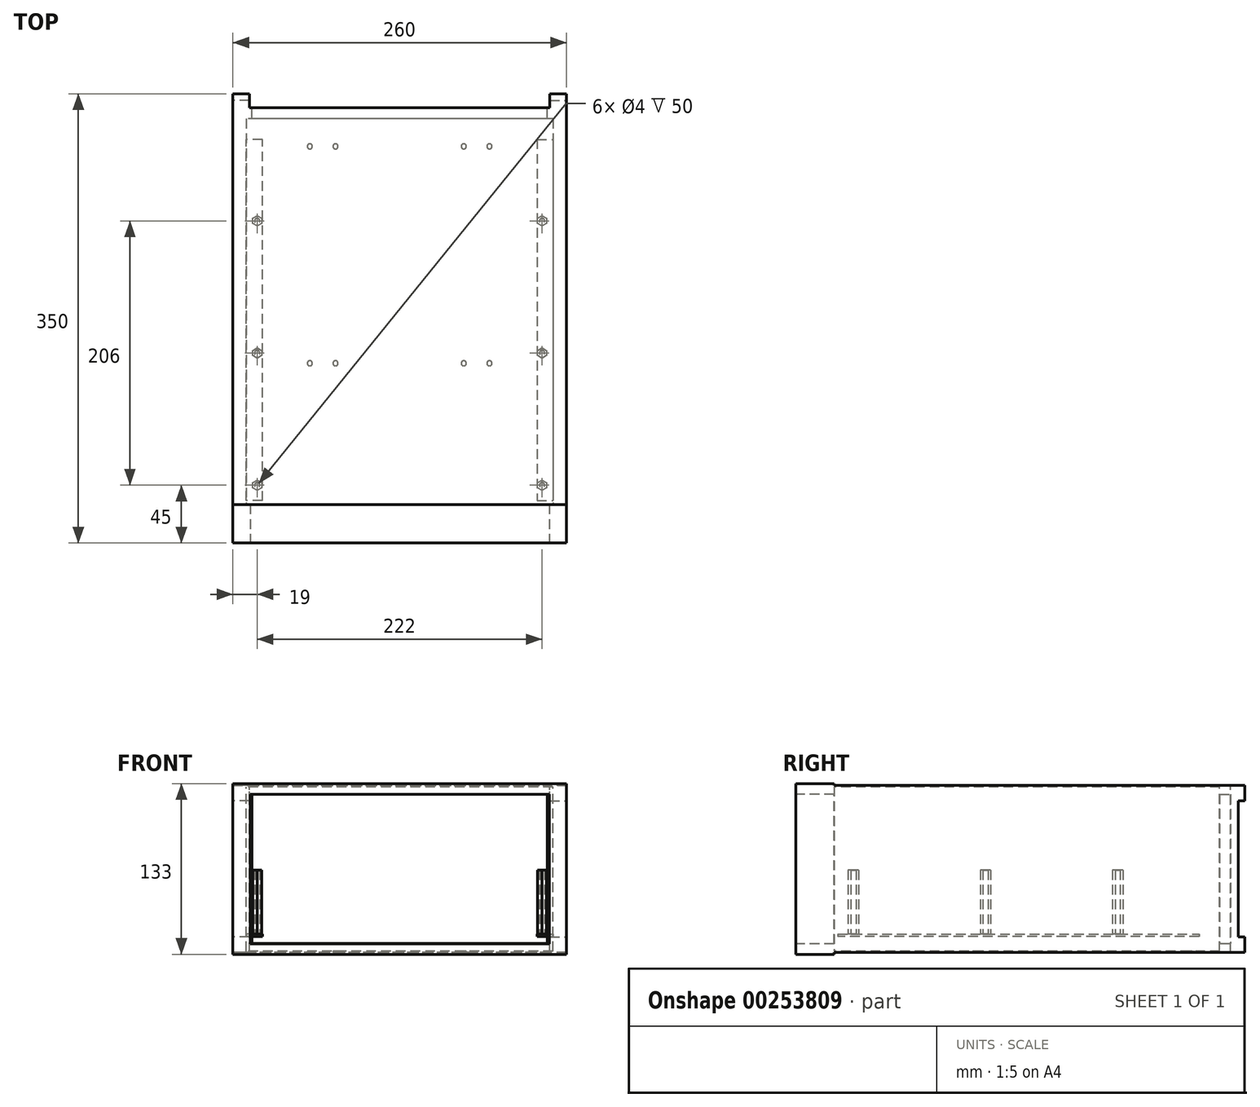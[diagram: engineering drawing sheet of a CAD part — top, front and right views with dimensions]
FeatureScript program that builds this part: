
annotation { "Feature Type Name" : "Feature", "Feature Type Description" : "" }
export const myFeature = defineFeature(function(context is Context, id is Id, definition is map)
    precondition{}
    {
        {
            var Q0;
            Q0=qCreatedBy(makeId("Top.planeOp"),FACE);
            var sketch = newSketch(context, id + "F0", { "sketchPlane" : qUnion([Q0])});
            skLineSegment(sketch, "E0.bottom", {"start": v(130, -175) * mm, "end": v(-130, -175) * mm});
            skLineSegment(sketch, "E0.top", {"start": v(130, 175) * mm, "end": v(-130, 175) * mm});
            skLineSegment(sketch, "E0.left", {"start": v(130, -175) * mm, "end": v(130, 175) * mm});
            skLineSegment(sketch, "E0.right", {"start": v(-130, -175) * mm, "end": v(-130, 175) * mm});
            skPoint(sketch, "E0.middle", {"position": v(0, 0) * mm});
            skSolve(sketch);
        }
        {
            var Q0;
            Q0=makeQuery(id+"F0.imprint","IMPRINT",FACE,{"disambiguationData":[TD([[makeQuery(id+"F0.imprint","IMPRINT",EDGE,{"derivedFrom":sQuery(id+"F0.wireOp",EDGE,"E0.bottom")}),-1.0]])]});
            extrude(context, id + "F1", {"entities" : qUnion([Q0]), "depth" : 133 * mm});
        }
        {
            var Q0;
            Q0=makeQuery(id+"F1.opExtrude","CAP_FACE",FACE,{"disambiguationData":[OSD([sQuery(id+"F0.wireOp",EDGE,"E0.bottom"),sQuery(id+"F0.wireOp",EDGE,"E0.top"),sQuery(id+"F0.wireOp",EDGE,"E0.left"),sQuery(id+"F0.wireOp",EDGE,"E0.right")])],"isStart":false});
            var sketch = newSketch(context, id + "F2", { "sketchPlane" : qUnion([Q0])});
            skLineSegment(sketch, "E1.bottom", {"start": v(-130, 175) * mm, "end": v(130, 175) * mm});
            skLineSegment(sketch, "E1.top", {"start": v(-130, -155) * mm, "end": v(130, -155) * mm});
            skLineSegment(sketch, "E1.left", {"start": v(-130, 175) * mm, "end": v(-130, -155) * mm});
            skLineSegment(sketch, "E1.right", {"start": v(130, 175) * mm, "end": v(130, -155) * mm});
            skSolve(sketch);
        }
        {
            var Q0;
            Q0=makeQuery(id+"F2.imprint","IMPRINT",FACE,{"disambiguationData":[TD([[makeQuery(id+"F2.imprint","IMPRINT",EDGE,{"derivedFrom":sQuery(id+"F2.wireOp",EDGE,"E1.bottom")}),1.0]])]});
            extrude(context, id + "F3", {"entities" : qUnion([Q0]), "operationType" : NewBodyOperationType.REMOVE, "oppositeDirection" : true, "depth" : 1.5 * mm});
        }
        {
            var Q0;
            Q0=makeQuery(id+"F1.opExtrude","CAP_FACE",FACE,{"disambiguationData":[OSD([sQuery(id+"F0.wireOp",EDGE,"E0.bottom"),sQuery(id+"F0.wireOp",EDGE,"E0.top"),sQuery(id+"F0.wireOp",EDGE,"E0.left"),sQuery(id+"F0.wireOp",EDGE,"E0.right")])],"isStart":true});
            var sketch = newSketch(context, id + "F4", { "sketchPlane" : qUnion([Q0])});
            skLineSegment(sketch, "E2.bottom", {"start": v(-130, -175) * mm, "end": v(130, -175) * mm});
            skLineSegment(sketch, "E2.top", {"start": v(-130, 155) * mm, "end": v(130, 155) * mm});
            skLineSegment(sketch, "E2.left", {"start": v(-130, -175) * mm, "end": v(-130, 155) * mm});
            skLineSegment(sketch, "E2.right", {"start": v(130, -175) * mm, "end": v(130, 155) * mm});
            skSolve(sketch);
        }
        {
            var Q0;
            Q0=makeQuery(id+"F4.imprint","IMPRINT",FACE,{"disambiguationData":[TD([[makeQuery(id+"F4.imprint","IMPRINT",EDGE,{"derivedFrom":sQuery(id+"F4.wireOp",EDGE,"E2.bottom")}),-1.0]])]});
            extrude(context, id + "F5", {"entities" : qUnion([Q0]), "operationType" : NewBodyOperationType.REMOVE, "oppositeDirection" : true, "depth" : 1.5 * mm});
        }
        {
            var Q0;
            Q0=makeQuery(id+"F3.boolean.opBoolean","COPY",FACE,{"derivedFrom":makeQuery(id+"F3.opExtrude","CAP_FACE",FACE,{"disambiguationData":[OSD([sQuery(id+"F2.wireOp",EDGE,"E1.bottom"),sQuery(id+"F2.wireOp",EDGE,"E1.top"),sQuery(id+"F2.wireOp",EDGE,"E1.left"),sQuery(id+"F2.wireOp",EDGE,"E1.right")])],"isStart":false})});
            var sketch = newSketch(context, id + "F6", { "sketchPlane" : qUnion([Q0])});
            skLineSegment(sketch, "E3.bottom", {"start": v(-117, 175) * mm, "end": v(117, 175) * mm});
            skLineSegment(sketch, "E3.top", {"start": v(-117, 164) * mm, "end": v(117, 164) * mm});
            skLineSegment(sketch, "E3.left", {"start": v(-117, 175) * mm, "end": v(-117, 164) * mm});
            skLineSegment(sketch, "E3.right", {"start": v(117, 175) * mm, "end": v(117, 164) * mm});
            skSolve(sketch);
        }
        {
            var Q0;
            Q0=makeQuery(id+"F6.imprint","IMPRINT",FACE,{"disambiguationData":[TD([[makeQuery(id+"F6.imprint","IMPRINT",EDGE,{"derivedFrom":sQuery(id+"F6.wireOp",EDGE,"E3.bottom")}),1.0]])]});
            extrude(context, id + "F7", {"entities" : qUnion([Q0]), "operationType" : NewBodyOperationType.REMOVE, "endBound" : BoundingType.THROUGH_ALL, "oppositeDirection" : true, "depth" : 25 * mm});
        }
        {
            var Q0;
            {var subQ0=sQuery(id+"F0.wireOp",EDGE,"E0.right");Q0=makeQuery(id+"F7.boolean.opBoolean","SPLIT",FACE,{"disambiguationData":[TD([makeQuery(id+"F1.opExtrude","SWEPT_FACE",FACE,{"disambiguationData":[OSD([subQ0])]})])],"derivedFrom":makeQuery(id+"F1.opExtrude","SWEPT_FACE",FACE,{"disambiguationData":[OSD([sQuery(id+"F0.wireOp",EDGE,"E0.top")])]})});}
            var sketch = newSketch(context, id + "F8", { "sketchPlane" : qUnion([Q0])});
            skLineSegment(sketch, "E4.bottom", {"start": v(117, 119.5) * mm, "end": v(130, 119.5) * mm});
            skLineSegment(sketch, "E4.top", {"start": v(117, 13.5) * mm, "end": v(130, 13.5) * mm});
            skLineSegment(sketch, "E4.left", {"start": v(117, 119.5) * mm, "end": v(117, 13.5) * mm});
            skLineSegment(sketch, "E4.right", {"start": v(130, 119.5) * mm, "end": v(130, 13.5) * mm});
            skSolve(sketch);
        }
        {
            var Q0;
            {var subQ0=sQuery(id+"F0.wireOp",EDGE,"E0.left");Q0=makeQuery(id+"F7.boolean.opBoolean","SPLIT",FACE,{"disambiguationData":[TD([makeQuery(id+"F1.opExtrude","SWEPT_FACE",FACE,{"disambiguationData":[OSD([subQ0])]})])],"derivedFrom":makeQuery(id+"F1.opExtrude","SWEPT_FACE",FACE,{"disambiguationData":[OSD([sQuery(id+"F0.wireOp",EDGE,"E0.top")])]})});}
            var sketch = newSketch(context, id + "F9", { "sketchPlane" : qUnion([Q0])});
            skLineSegment(sketch, "E5.bottom", {"start": v(-117, 119.5) * mm, "end": v(-130, 119.5) * mm});
            skLineSegment(sketch, "E5.top", {"start": v(-117, 13.5) * mm, "end": v(-130, 13.5) * mm});
            skLineSegment(sketch, "E5.left", {"start": v(-117, 119.5) * mm, "end": v(-117, 13.5) * mm});
            skLineSegment(sketch, "E5.right", {"start": v(-130, 119.5) * mm, "end": v(-130, 13.5) * mm});
            skSolve(sketch);
        }
        {
            var Q0;
            Q0=makeQuery(id+"F5.boolean.opBoolean","COPY",FACE,{"derivedFrom":makeQuery(id+"F5.opExtrude","CAP_FACE",FACE,{"disambiguationData":[OSD([sQuery(id+"F4.wireOp",EDGE,"E2.bottom"),sQuery(id+"F4.wireOp",EDGE,"E2.top"),sQuery(id+"F4.wireOp",EDGE,"E2.left"),sQuery(id+"F4.wireOp",EDGE,"E2.right")])],"isStart":false})});
            var sketch = newSketch(context, id + "F10", { "sketchPlane" : qUnion([Q0])});
            skCircle(sketch, "E6", {"center": v(70, 35) * mm, "radius": 2 * mm});
            skCircle(sketch, "E7", {"center": v(50, 35) * mm, "radius": 2 * mm});
            skCircle(sketch, "E8", {"center": v(-70, 35) * mm, "radius": 2 * mm});
            skCircle(sketch, "E9", {"center": v(-50, 35) * mm, "radius": 2 * mm});
            skCircle(sketch, "E10", {"center": v(70, -134) * mm, "radius": 2 * mm});
            skCircle(sketch, "E11", {"center": v(50, -134) * mm, "radius": 2 * mm});
            skCircle(sketch, "E12", {"center": v(-50, -134) * mm, "radius": 2 * mm});
            skCircle(sketch, "E13", {"center": v(-70, -134) * mm, "radius": 2 * mm});
            skSolve(sketch);
        }
        {
            var Q0;
            Q0 = qSketchRegion(id + "F10", true);
            extrude(context, id + "F11", {"entities" : qUnion([Q0]), "operationType" : NewBodyOperationType.REMOVE, "oppositeDirection" : true, "depth" : 25 * mm});
        }
        {
            var Q0;
            Q0=makeQuery(id+"F1.opExtrude","SWEPT_FACE",FACE,{"disambiguationData":[OSD([sQuery(id+"F0.wireOp",EDGE,"E0.bottom")])]});
            var sketch = newSketch(context, id + "F12", { "sketchPlane" : qUnion([Q0])});
            skPoint(sketch, "E14", {"position": v(0, 66.5) * mm});
            skLineSegment(sketch, "E15.bottom", {"start": v(119.5, 2.5) * mm, "end": v(-119.5, 2.5) * mm});
            skLineSegment(sketch, "E15.top", {"start": v(119.5, 130.5) * mm, "end": v(-119.5, 130.5) * mm});
            skLineSegment(sketch, "E15.left", {"start": v(119.5, 2.5) * mm, "end": v(119.5, 130.5) * mm});
            skLineSegment(sketch, "E15.right", {"start": v(-119.5, 2.5) * mm, "end": v(-119.5, 130.5) * mm});
            skSolve(sketch);
        }
        {
            var Q0;
            Q0=makeQuery(id+"F12.imprint","IMPRINT",FACE,{"disambiguationData":[TD([[makeQuery(id+"F12.imprint","IMPRINT",EDGE,{"derivedFrom":sQuery(id+"F12.wireOp",EDGE,"E15.bottom")}),-1.0]])]});
            extrude(context, id + "F13", {"entities" : qUnion([Q0]), "operationType" : NewBodyOperationType.REMOVE, "oppositeDirection" : true, "depth" : 330.5 * mm});
        }
        {
            var Q0;
            Q0=makeQuery(id+"F1.opExtrude","SWEPT_FACE",FACE,{"disambiguationData":[OSD([sQuery(id+"F0.wireOp",EDGE,"E0.bottom")])]});
            var sketch = newSketch(context, id + "F14", { "sketchPlane" : qUnion([Q0])});
            skLineSegment(sketch, "E16.bottom", {"start": v(-130, 133) * mm, "end": v(130, 133) * mm});
            skLineSegment(sketch, "E16.top", {"start": v(-130, 0) * mm, "end": v(130, 0) * mm});
            skLineSegment(sketch, "E16.left", {"start": v(-130, 133) * mm, "end": v(-130, 0) * mm});
            skLineSegment(sketch, "E16.right", {"start": v(130, 133) * mm, "end": v(130, 0) * mm});
            skPoint(sketch, "E17", {"position": v(0, 66.5) * mm});
            skLineSegment(sketch, "E18.bottom", {"start": v(116.5, 8.25) * mm, "end": v(-116.5, 8.25) * mm});
            skLineSegment(sketch, "E18.top", {"start": v(116.5, 124.75) * mm, "end": v(-116.5, 124.75) * mm});
            skLineSegment(sketch, "E18.left", {"start": v(116.5, 8.25) * mm, "end": v(116.5, 124.75) * mm});
            skLineSegment(sketch, "E18.right", {"start": v(-116.5, 8.25) * mm, "end": v(-116.5, 124.75) * mm});
            skSolve(sketch);
        }
        {
            var Q0;
            Q0 = qSketchRegion(id + "F14", true);
            extrude(context, id + "F15", {"entities" : qUnion([Q0]), "operationType" : NewBodyOperationType.ADD, "oppositeDirection" : true, "depth" : 30 * mm});
        }
        {
            var Q0;
            Q0=makeQuery(id+"F9.imprint","IMPRINT",FACE,{"disambiguationData":[TD([[makeQuery(id+"F9.imprint","IMPRINT",EDGE,{"derivedFrom":sQuery(id+"F9.wireOp",EDGE,"E5.bottom")}),1.0]])]});
            var Q1;
            Q1=makeQuery(id+"F8.imprint","IMPRINT",FACE,{"disambiguationData":[TD([[makeQuery(id+"F8.imprint","IMPRINT",EDGE,{"derivedFrom":sQuery(id+"F8.wireOp",EDGE,"E4.bottom")}),-1.0]])]});
            extrude(context, id + "F16", {"entities" : qUnion([Q0, Q1]), "operationType" : NewBodyOperationType.REMOVE, "oppositeDirection" : true, "depth" : 5 * mm});
        }
        {
            var Q0;
            Q0=makeQuery(id+"F8.imprint","IMPRINT",FACE,{"disambiguationData":[TD([[makeQuery(id+"F8.imprint","IMPRINT",EDGE,{"derivedFrom":sQuery(id+"F8.wireOp",EDGE,"E4.bottom")}),-1.0]])]});
            var sketch = newSketch(context, id + "F17", { "sketchPlane" : qUnion([Q0])});
            skPoint(sketch, "E19", {"position": v(0, 66.5) * mm});
            skLineSegment(sketch, "E20.bottom", {"start": v(115, 8.38) * mm, "end": v(-115, 8.37) * mm});
            skLineSegment(sketch, "E20.top", {"start": v(115, 124.63) * mm, "end": v(-115, 124.62) * mm});
            skLineSegment(sketch, "E20.left", {"start": v(115, 8.38) * mm, "end": v(115, 124.63) * mm});
            skLineSegment(sketch, "E20.right", {"start": v(-115, 8.37) * mm, "end": v(-115, 124.62) * mm});
            skSolve(sketch);
        }
        {
            var Q0;
            Q0 = qSketchRegion(id + "F17", true);
            extrude(context, id + "F18", {"entities" : qUnion([Q0]), "operationType" : NewBodyOperationType.REMOVE, "oppositeDirection" : true, "depth" : 25 * mm});
        }
        {
            var Q0;
            Q0=makeQuery(id+"F13.boolean.opBoolean","COPY",FACE,{"derivedFrom":makeQuery(id+"F13.opExtrude","SWEPT_FACE",FACE,{"disambiguationData":[OSD([sQuery(id+"F12.wireOp",EDGE,"E15.right")])]})});
            var sketch = newSketch(context, id + "F19", { "sketchPlane" : qUnion([Q0])});
            skLineSegment(sketch, "E21.bottom", {"start": v(-142, 15.6) * mm, "end": v(139.5, 15.6) * mm});
            skLineSegment(sketch, "E21.top", {"start": v(-142, 14) * mm, "end": v(139.5, 14) * mm});
            skLineSegment(sketch, "E21.left", {"start": v(-142, 15.6) * mm, "end": v(-142, 14) * mm});
            skLineSegment(sketch, "E21.right", {"start": v(139.5, 15.6) * mm, "end": v(139.5, 14) * mm});
            skSolve(sketch);
        }
        {
            var Q0;
            Q0 = qSketchRegion(id + "F19", true);
            extrude(context, id + "F20", {"entities" : qUnion([Q0]), "operationType" : NewBodyOperationType.ADD, "depth" : 12.5 * mm});
        }
        {
            var Q0;
            Q0=makeQuery(id+"F13.boolean.opBoolean","COPY",FACE,{"derivedFrom":makeQuery(id+"F13.opExtrude","SWEPT_FACE",FACE,{"disambiguationData":[OSD([sQuery(id+"F12.wireOp",EDGE,"E15.left")])]})});
            var sketch = newSketch(context, id + "F21", { "sketchPlane" : qUnion([Q0])});
            skLineSegment(sketch, "E22.bottom", {"start": v(-139.5, 15.6) * mm, "end": v(142, 15.6) * mm});
            skLineSegment(sketch, "E22.top", {"start": v(-139.5, 14) * mm, "end": v(142, 14) * mm});
            skLineSegment(sketch, "E22.left", {"start": v(-139.5, 15.6) * mm, "end": v(-139.5, 14) * mm});
            skLineSegment(sketch, "E22.right", {"start": v(142, 15.6) * mm, "end": v(142, 14) * mm});
            skSolve(sketch);
        }
        {
            var Q0;
            Q0 = qSketchRegion(id + "F21", true);
            extrude(context, id + "F22", {"entities" : qUnion([Q0]), "operationType" : NewBodyOperationType.ADD, "depth" : 12.5 * mm});
        }
        {
            var Q0;
            Q0=makeQuery(id+"F22.opExtrude","SWEPT_FACE",FACE,{"disambiguationData":[OSD([sQuery(id+"F21.wireOp",EDGE,"E22.bottom")])]});
            var sketch = newSketch(context, id + "F23", { "sketchPlane" : qUnion([Q0])});
            skCircle(sketch, "E23.cCircle", {"center": v(111, -130) * mm, "radius": 3.5 * mm, "construction": true});
            skLineSegment(sketch, "E23.0", {"start": v(114.5, -132.02) * mm, "end": v(111, -134.04) * mm});
            skLineSegment(sketch, "E23.1", {"start": v(111, -134.04) * mm, "end": v(107.5, -132.02) * mm});
            skLineSegment(sketch, "E23.2", {"start": v(107.5, -132.02) * mm, "end": v(107.5, -127.98) * mm});
            skLineSegment(sketch, "E23.3", {"start": v(107.5, -127.98) * mm, "end": v(111, -125.96) * mm});
            skLineSegment(sketch, "E23.4", {"start": v(111, -125.96) * mm, "end": v(114.5, -127.98) * mm});
            skLineSegment(sketch, "E23.5", {"start": v(114.5, -127.98) * mm, "end": v(114.5, -132.02) * mm});
            skPoint(sketch, "E23.0.midPoint", {"position": v(112.75, -133.03) * mm});
            skCircle(sketch, "E24.cCircle", {"center": v(111, 76) * mm, "radius": 3.5 * mm, "construction": true});
            skLineSegment(sketch, "E24.0", {"start": v(114.5, 73.98) * mm, "end": v(111, 71.96) * mm});
            skLineSegment(sketch, "E24.1", {"start": v(111, 71.96) * mm, "end": v(107.5, 73.98) * mm});
            skLineSegment(sketch, "E24.2", {"start": v(107.5, 73.98) * mm, "end": v(107.5, 78.02) * mm});
            skLineSegment(sketch, "E24.3", {"start": v(107.5, 78.02) * mm, "end": v(111, 80.04) * mm});
            skLineSegment(sketch, "E24.4", {"start": v(111, 80.04) * mm, "end": v(114.5, 78.02) * mm});
            skLineSegment(sketch, "E24.5", {"start": v(114.5, 78.02) * mm, "end": v(114.5, 73.98) * mm});
            skPoint(sketch, "E24.0.midPoint", {"position": v(112.75, 72.97) * mm});
            skCircle(sketch, "E25.cCircle", {"center": v(111, -27) * mm, "radius": 3.5 * mm, "construction": true});
            skLineSegment(sketch, "E25.0", {"start": v(114.5, -29.02) * mm, "end": v(111, -31.04) * mm});
            skLineSegment(sketch, "E25.1", {"start": v(111, -31.04) * mm, "end": v(107.5, -29.02) * mm});
            skLineSegment(sketch, "E25.2", {"start": v(107.5, -29.02) * mm, "end": v(107.5, -24.98) * mm});
            skLineSegment(sketch, "E25.3", {"start": v(107.5, -24.98) * mm, "end": v(111, -22.96) * mm});
            skLineSegment(sketch, "E25.4", {"start": v(111, -22.96) * mm, "end": v(114.5, -24.98) * mm});
            skLineSegment(sketch, "E25.5", {"start": v(114.5, -24.98) * mm, "end": v(114.5, -29.02) * mm});
            skPoint(sketch, "E25.0.midPoint", {"position": v(112.75, -30.03) * mm});
            skCircle(sketch, "E26.cCircle", {"center": v(-111, -130) * mm, "radius": 3.5 * mm, "construction": true});
            skLineSegment(sketch, "E26.0", {"start": v(-107.5, -132.02) * mm, "end": v(-111, -134.04) * mm});
            skLineSegment(sketch, "E26.1", {"start": v(-111, -134.04) * mm, "end": v(-114.5, -132.02) * mm});
            skLineSegment(sketch, "E26.2", {"start": v(-114.5, -132.02) * mm, "end": v(-114.5, -127.98) * mm});
            skLineSegment(sketch, "E26.3", {"start": v(-114.5, -127.98) * mm, "end": v(-111, -125.96) * mm});
            skLineSegment(sketch, "E26.4", {"start": v(-111, -125.96) * mm, "end": v(-107.5, -127.98) * mm});
            skLineSegment(sketch, "E26.5", {"start": v(-107.5, -127.98) * mm, "end": v(-107.5, -132.02) * mm});
            skPoint(sketch, "E26.0.midPoint", {"position": v(-109.25, -133.03) * mm});
            skCircle(sketch, "E27.cCircle", {"center": v(-111, -27) * mm, "radius": 3.5 * mm, "construction": true});
            skLineSegment(sketch, "E27.0", {"start": v(-107.5, -24.98) * mm, "end": v(-107.5, -29.02) * mm});
            skLineSegment(sketch, "E27.1", {"start": v(-107.5, -29.02) * mm, "end": v(-111, -31.04) * mm});
            skLineSegment(sketch, "E27.2", {"start": v(-111, -31.04) * mm, "end": v(-114.5, -29.02) * mm});
            skLineSegment(sketch, "E27.3", {"start": v(-114.5, -29.02) * mm, "end": v(-114.5, -24.98) * mm});
            skLineSegment(sketch, "E27.4", {"start": v(-114.5, -24.98) * mm, "end": v(-111, -22.96) * mm});
            skLineSegment(sketch, "E27.5", {"start": v(-111, -22.96) * mm, "end": v(-107.5, -24.98) * mm});
            skPoint(sketch, "E27.0.midPoint", {"position": v(-107.5, -27) * mm});
            skCircle(sketch, "E28.cCircle", {"center": v(-111, 76) * mm, "radius": 3.5 * mm, "construction": true});
            skLineSegment(sketch, "E28.0", {"start": v(-107.5, 73.98) * mm, "end": v(-111, 71.96) * mm});
            skLineSegment(sketch, "E28.1", {"start": v(-111, 71.96) * mm, "end": v(-114.5, 73.98) * mm});
            skLineSegment(sketch, "E28.2", {"start": v(-114.5, 73.98) * mm, "end": v(-114.5, 78.02) * mm});
            skLineSegment(sketch, "E28.3", {"start": v(-114.5, 78.02) * mm, "end": v(-111, 80.04) * mm});
            skLineSegment(sketch, "E28.4", {"start": v(-111, 80.04) * mm, "end": v(-107.5, 78.02) * mm});
            skLineSegment(sketch, "E28.5", {"start": v(-107.5, 78.02) * mm, "end": v(-107.5, 73.98) * mm});
            skPoint(sketch, "E28.0.midPoint", {"position": v(-109.25, 72.97) * mm});
            skCircle(sketch, "E29", {"center": v(-111, -130) * mm, "radius": 2 * mm});
            skCircle(sketch, "E30", {"center": v(-111, -27) * mm, "radius": 2 * mm});
            skCircle(sketch, "E31", {"center": v(-111, 76) * mm, "radius": 2 * mm});
            skCircle(sketch, "E32", {"center": v(111, 76) * mm, "radius": 2 * mm});
            skCircle(sketch, "E33", {"center": v(111, -27) * mm, "radius": 2 * mm});
            skCircle(sketch, "E34", {"center": v(111, -130) * mm, "radius": 2 * mm});
            skSolve(sketch);
        }
        {
            var Q0;
            Q0 = qSketchRegion(id + "F23", true);
            extrude(context, id + "F24", {"entities" : qUnion([Q0]), "operationType" : NewBodyOperationType.ADD, "depth" : 50 * mm});
        }
    });
